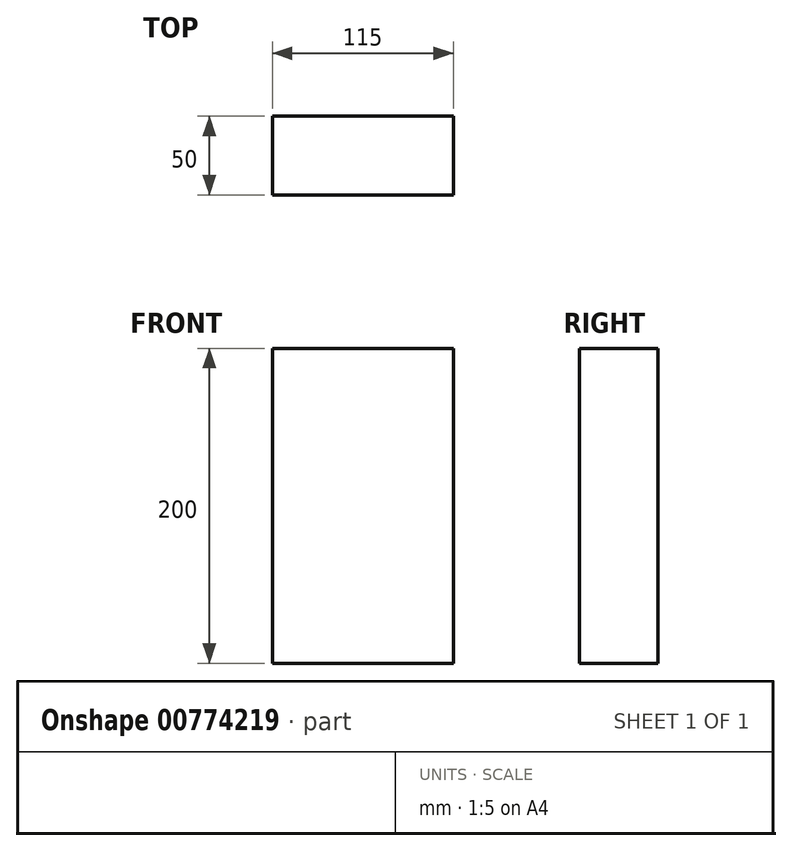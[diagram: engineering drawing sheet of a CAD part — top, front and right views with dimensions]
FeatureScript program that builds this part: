
annotation { "Feature Type Name" : "Feature", "Feature Type Description" : "" }
export const myFeature = defineFeature(function(context is Context, id is Id, definition is map)
    precondition{}
    {
        {
            var Q0;
            Q0=qCreatedBy(makeId("Top.planeOp"),FACE);
            var sketch = newSketch(context, id + "F0", { "sketchPlane" : qUnion([Q0])});
            skLineSegment(sketch, "E0.bottom", {"start": v(-57.5, 25) * mm, "end": v(57.5, 25) * mm});
            skLineSegment(sketch, "E0.top", {"start": v(-57.5, -25) * mm, "end": v(57.5, -25) * mm});
            skLineSegment(sketch, "E0.left", {"start": v(-57.5, 25) * mm, "end": v(-57.5, -25) * mm});
            skLineSegment(sketch, "E0.right", {"start": v(57.5, 25) * mm, "end": v(57.5, -25) * mm});
            skPoint(sketch, "E0.middle", {"position": v(0, 0) * mm});
            skSolve(sketch);
        }
        {
            var Q0;
            Q0=makeQuery(id+"F0.imprint","IMPRINT",FACE,{"disambiguationData":[TD([[makeQuery(id+"F0.imprint","IMPRINT",EDGE,{"derivedFrom":sQuery(id+"F0.wireOp",EDGE,"E0.bottom")}),-1.0]])]});
            extrude(context, id + "F1", {"entities" : qUnion([Q0]), "depth" : 200 * mm, "offsetDistance" : 25 * mm});
        }
    });
